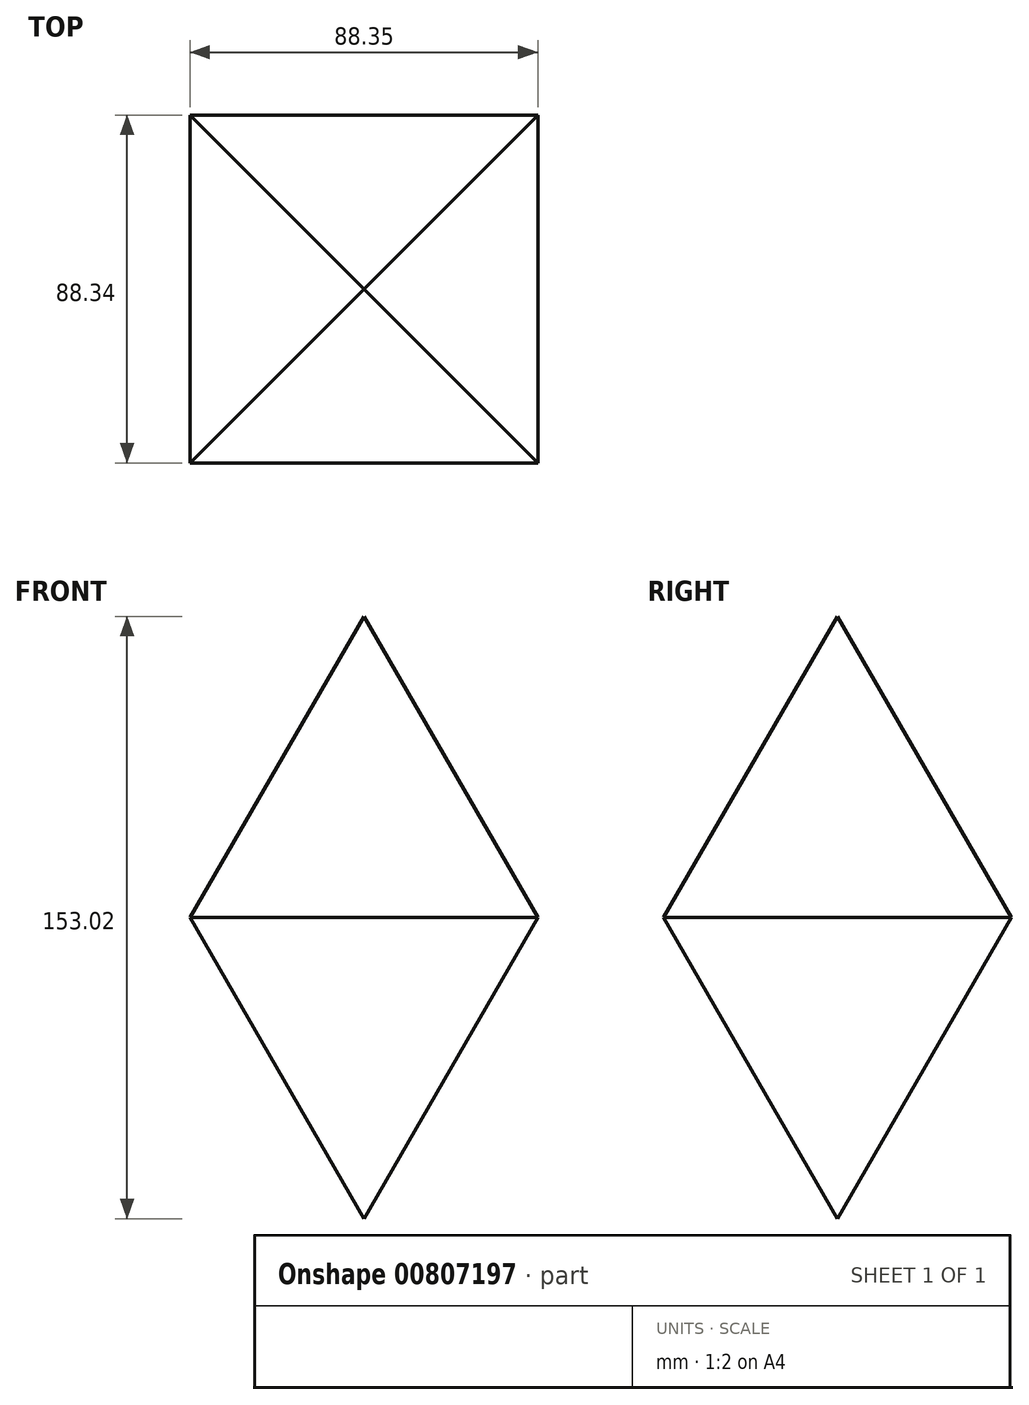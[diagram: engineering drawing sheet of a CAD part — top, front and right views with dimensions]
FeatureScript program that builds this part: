
annotation { "Feature Type Name" : "Feature", "Feature Type Description" : "" }
export const myFeature = defineFeature(function(context is Context, id is Id, definition is map)
    precondition{}
    {
        {
            var Q0;
            Q0=qCreatedBy(makeId("Top.planeOp"),FACE);
            var sketch = newSketch(context, id + "F0", { "sketchPlane" : qUnion([Q0])});
            skLineSegment(sketch, "E0.bottom", {"start": v(-25.7, -20.1) * mm, "end": v(62.64, -20.1) * mm});
            skLineSegment(sketch, "E0.top", {"start": v(-25.7, 68.24) * mm, "end": v(62.64, 68.24) * mm});
            skLineSegment(sketch, "E0.left", {"start": v(-25.7, -20.1) * mm, "end": v(-25.7, 68.24) * mm});
            skLineSegment(sketch, "E0.right", {"start": v(62.64, -20.1) * mm, "end": v(62.64, 68.24) * mm});
            skPoint(sketch, "E0.middle", {"position": v(18.46, 24.07) * mm});
            skSolve(sketch);
        }
        {
            var Q0;
            Q0=makeQuery(id+"F0.imprint","IMPRINT",FACE,{"disambiguationData":[TD([[makeQuery(id+"F0.imprint","IMPRINT",EDGE,{"derivedFrom":sQuery(id+"F0.wireOp",EDGE,"E0.bottom")}),1.0]])]});
            extrude(context, id + "F1", {"entities" : qUnion([Q0]), "depth" : 146.05 * mm, "offsetDistance" : 25.4 * mm, "hasDraft" : true, "draftAngle" : 30 * degree, "draftPullDirection" : true, "hasSecondDirection" : true, "secondDirectionOppositeDirection" : true, "secondDirectionDepth" : 165.6 * mm, "hasSecondDirectionDraft" : true, "secondDirectionDraftAngle" : 30 * degree, "secondDirectionDraftPullDirection" : true});
        }
    });
